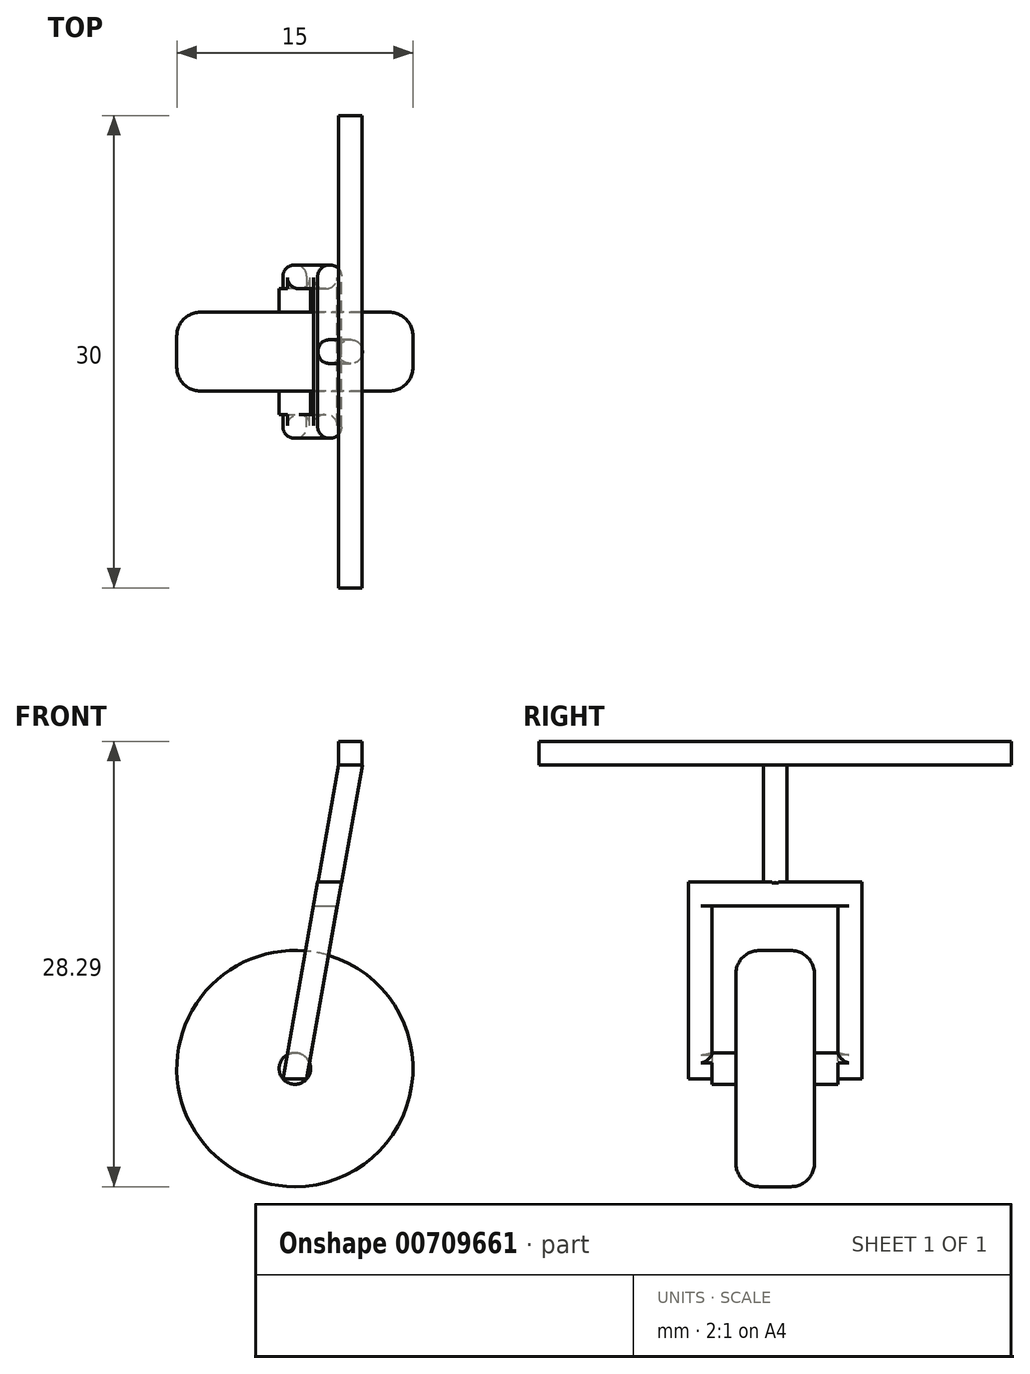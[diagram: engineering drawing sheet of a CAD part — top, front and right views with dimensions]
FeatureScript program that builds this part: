
annotation { "Feature Type Name" : "Feature", "Feature Type Description" : "" }
export const myFeature = defineFeature(function(context is Context, id is Id, definition is map)
    precondition{}
    {
        {
            var Q0;
            Q0=qCreatedBy(makeId("Front.planeOp"),FACE);
            var sketch = newSketch(context, id + "F0", { "sketchPlane" : qUnion([Q0])});
            skLineSegment(sketch, "E0.bottom", {"start": v(-45.66, 5.93) * mm, "end": v(-30.66, 5.93) * mm});
            skLineSegment(sketch, "E0.top", {"start": v(-45.66, -9.07) * mm, "end": v(-30.66, -9.07) * mm});
            skLineSegment(sketch, "E0.left", {"start": v(-45.66, 5.93) * mm, "end": v(-45.66, -9.07) * mm});
            skLineSegment(sketch, "E0.right", {"start": v(-30.66, 5.93) * mm, "end": v(-30.66, -9.07) * mm});
            skSolve(sketch);
        }
        {
            var Q0;
            Q0=makeQuery(id+"F0.imprint","IMPRINT",FACE,{"disambiguationData":[TD([[makeQuery(id+"F0.imprint","IMPRINT",EDGE,{"derivedFrom":sQuery(id+"F0.wireOp",EDGE,"E0.bottom")}),-1.0]])]});
            extrude(context, id + "F1", {"entities" : qUnion([Q0]), "endBound" : BoundingType.SYMMETRIC, "depth" : 5 * mm, "offsetDistance" : 25 * mm});
        }
        {
            var Q0;
            Q0=makeQuery(id+"F1.opExtrude","SWEPT_EDGE",EDGE,{"disambiguationData":[OSD([sQuery(id+"F0.wireOp",EDGE,"E0.bottom"),sQuery(id+"F0.wireOp",EDGE,"E0.right")])]});
            var Q1;
            Q1=makeQuery(id+"F1.opExtrude","SWEPT_EDGE",EDGE,{"disambiguationData":[OSD([sQuery(id+"F0.wireOp",EDGE,"E0.bottom"),sQuery(id+"F0.wireOp",EDGE,"E0.left")])]});
            var Q2;
            Q2=makeQuery(id+"F1.opExtrude","SWEPT_EDGE",EDGE,{"disambiguationData":[OSD([sQuery(id+"F0.wireOp",EDGE,"E0.top"),sQuery(id+"F0.wireOp",EDGE,"E0.right")])]});
            var Q3;
            Q3=makeQuery(id+"F1.opExtrude","SWEPT_EDGE",EDGE,{"disambiguationData":[OSD([sQuery(id+"F0.wireOp",EDGE,"E0.top"),sQuery(id+"F0.wireOp",EDGE,"E0.left")])]});
            fillet(context, id + "F2", {"entities" : qUnion([Q0, Q1, Q2, Q3]), "radius" : 7.5 * mm, "tangentPropagation" : true, "allowEdgeOverflow" : false});
        }
        {
            var Q0;
            {var subQ0=sQuery(id+"F0.wireOp",EDGE,"E0.left");var subQ1=sQuery(id+"F0.wireOp",EDGE,"E0.bottom");Q0=makeQuery(id+"F2.opFillet","BLEND_EDGE",EDGE,{"blendedFrom":[makeQuery(id+"F1.opExtrude","SWEPT_EDGE",EDGE,{"disambiguationData":[OSD([subQ1,subQ0])]}),makeQuery(id+"F1.opExtrude","CAP_FACE",FACE,{"disambiguationData":[OSD([subQ1,sQuery(id+"F0.wireOp",EDGE,"E0.top"),subQ0,sQuery(id+"F0.wireOp",EDGE,"E0.right")])],"isStart":false})],"blendedInto":[makeQuery(id+"F1.opExtrude","CAP_FACE",FACE,{"disambiguationData":[OSD([subQ1,sQuery(id+"F0.wireOp",EDGE,"E0.top"),subQ0,sQuery(id+"F0.wireOp",EDGE,"E0.right")])],"isStart":false})]});}
            var Q1;
            {var subQ0=sQuery(id+"F0.wireOp",EDGE,"E0.left");var subQ1=sQuery(id+"F0.wireOp",EDGE,"E0.bottom");Q1=makeQuery(id+"F2.opFillet","BLEND_EDGE",EDGE,{"blendedFrom":[makeQuery(id+"F1.opExtrude","SWEPT_EDGE",EDGE,{"disambiguationData":[OSD([subQ1,subQ0])]}),makeQuery(id+"F1.opExtrude","CAP_FACE",FACE,{"disambiguationData":[OSD([subQ1,sQuery(id+"F0.wireOp",EDGE,"E0.top"),subQ0,sQuery(id+"F0.wireOp",EDGE,"E0.right")])],"isStart":true})],"blendedInto":[makeQuery(id+"F1.opExtrude","CAP_FACE",FACE,{"disambiguationData":[OSD([subQ1,sQuery(id+"F0.wireOp",EDGE,"E0.top"),subQ0,sQuery(id+"F0.wireOp",EDGE,"E0.right")])],"isStart":true})]});}
            fillet(context, id + "F3", {"entities" : qUnion([Q0, Q1]), "radius" : 1.5 * mm, "tangentPropagation" : true, "allowEdgeOverflow" : false});
        }
        {
            var Q0;
            Q0=makeQuery(id+"F1.opExtrude","CAP_FACE",FACE,{"disambiguationData":[OSD([sQuery(id+"F0.wireOp",EDGE,"E0.bottom"),sQuery(id+"F0.wireOp",EDGE,"E0.top"),sQuery(id+"F0.wireOp",EDGE,"E0.left"),sQuery(id+"F0.wireOp",EDGE,"E0.right")])],"isStart":false});
            var sketch = newSketch(context, id + "F4", { "sketchPlane" : qUnion([Q0])});
            skCircle(sketch, "E1", {"center": v(-38.16, -1.57) * mm, "radius": 1 * mm});
            skSolve(sketch);
        }
        {
            var Q0;
            Q0=makeQuery(id+"F4.imprint","IMPRINT",FACE,{"disambiguationData":[TD([[makeQuery(id+"F4.imprint","IMPRINT",EDGE,{"derivedFrom":sQuery(id+"F4.wireOp",EDGE,"E1")}),1.0]])]});
            extrude(context, id + "F5", {"entities" : qUnion([Q0]), "operationType" : NewBodyOperationType.ADD, "depth" : 1.5 * mm, "offsetDistance" : 25 * mm});
        }
        {
            var Q0;
            Q0=makeQuery(id+"F5.opExtrude","CAP_FACE",FACE,{"disambiguationData":[OSD([sQuery(id+"F4.wireOp",EDGE,"E1")])],"isStart":false});
            var sketch = newSketch(context, id + "F6", { "sketchPlane" : qUnion([Q0])});
            skLineSegment(sketch, "E2", {"start": v(-35.21, 10.27) * mm, "end": v(-36.71, 10.27) * mm});
            skLineSegment(sketch, "E3", {"start": v(-38.91, -2.23) * mm, "end": v(-37.41, -2.23) * mm});
            skLineSegment(sketch, "E4", {"start": v(-37.41, -2.23) * mm, "end": v(-35.21, 10.27) * mm});
            skLineSegment(sketch, "E5", {"start": v(-38.91, -2.23) * mm, "end": v(-36.71, 10.27) * mm});
            skSolve(sketch);
        }
        {
            var Q0;
            {var subQ0=sQuery(id+"F6.wireOp",EDGE,"E2");Q0=makeQuery(id+"F6.imprint","IMPRINT",FACE,{"disambiguationData":[TD([[makeQuery(id+"F6.imprint","IMPRINT",EDGE,{"derivedFrom":subQ0}),1.0]])]});}
            var Q1;
            {var subQ0=sQuery(id+"F6.wireOp",EDGE,"E3");Q1=makeQuery(id+"F6.imprint","IMPRINT",FACE,{"disambiguationData":[TD([[makeQuery(id+"F6.imprint","IMPRINT",EDGE,{"derivedFrom":subQ0}),1.0]])]});}
            extrude(context, id + "F7", {"entities" : qUnion([Q0, Q1]), "operationType" : NewBodyOperationType.ADD, "depth" : 1.5 * mm, "offsetDistance" : 25 * mm});
        }
        {
            var Q0;
            Q0=makeQuery(id+"F1.opExtrude","CAP_FACE",FACE,{"disambiguationData":[OSD([sQuery(id+"F0.wireOp",EDGE,"E0.bottom"),sQuery(id+"F0.wireOp",EDGE,"E0.top"),sQuery(id+"F0.wireOp",EDGE,"E0.left"),sQuery(id+"F0.wireOp",EDGE,"E0.right")])],"isStart":true});
            var sketch = newSketch(context, id + "F8", { "sketchPlane" : qUnion([Q0])});
            skCircle(sketch, "E6", {"center": v(38.16, -1.57) * mm, "radius": 1 * mm});
            skSolve(sketch);
        }
        {
            var Q0;
            Q0=makeQuery(id+"F8.imprint","IMPRINT",FACE,{"disambiguationData":[TD([[makeQuery(id+"F8.imprint","IMPRINT",EDGE,{"derivedFrom":sQuery(id+"F8.wireOp",EDGE,"E6")}),1.0]])]});
            extrude(context, id + "F9", {"entities" : qUnion([Q0]), "operationType" : NewBodyOperationType.ADD, "depth" : 1.5 * mm, "offsetDistance" : 25 * mm});
        }
        {
            var Q0;
            Q0=makeQuery(id+"F9.opExtrude","CAP_FACE",FACE,{"disambiguationData":[OSD([sQuery(id+"F8.wireOp",EDGE,"E6")])],"isStart":false});
            var sketch = newSketch(context, id + "F10", { "sketchPlane" : qUnion([Q0])});
            skLineSegment(sketch, "E7", {"start": v(37.41, -2.23) * mm, "end": v(38.91, -2.23) * mm});
            skLineSegment(sketch, "E8", {"start": v(38.91, -2.23) * mm, "end": v(36.71, 10.27) * mm});
            skLineSegment(sketch, "E9", {"start": v(36.71, 10.27) * mm, "end": v(35.21, 10.27) * mm});
            skLineSegment(sketch, "E10", {"start": v(35.21, 10.27) * mm, "end": v(37.41, -2.23) * mm});
            skSolve(sketch);
        }
        {
            var Q0;
            {var subQ0=sQuery(id+"F10.wireOp",EDGE,"E9");Q0=makeQuery(id+"F10.imprint","IMPRINT",FACE,{"disambiguationData":[TD([[makeQuery(id+"F10.imprint","IMPRINT",EDGE,{"derivedFrom":subQ0}),1.0]])]});}
            var Q1;
            {var subQ0=sQuery(id+"F10.wireOp",EDGE,"E7");Q1=makeQuery(id+"F10.imprint","IMPRINT",FACE,{"disambiguationData":[TD([[makeQuery(id+"F10.imprint","IMPRINT",EDGE,{"derivedFrom":subQ0}),1.0]])]});}
            extrude(context, id + "F11", {"entities" : qUnion([Q0, Q1]), "operationType" : NewBodyOperationType.ADD, "depth" : 1.5 * mm, "offsetDistance" : 25 * mm});
        }
        {
            var Q0;
            Q0=makeQuery(id+"F11.opExtrude","CAP_FACE",FACE,{"disambiguationData":[OSD([sQuery(id+"F10.wireOp",EDGE,"E7"),sQuery(id+"F10.wireOp",EDGE,"E8"),sQuery(id+"F10.wireOp",EDGE,"E9"),sQuery(id+"F10.wireOp",EDGE,"E10")])],"isStart":true});
            var sketch = newSketch(context, id + "F12", { "sketchPlane" : qUnion([Q0])});
            skLineSegment(sketch, "E11.bottom", {"start": v(-36.71, 10.27) * mm, "end": v(-35.21, 10.27) * mm});
            skLineSegment(sketch, "E11.top", {"start": v(-36.97, 8.77) * mm, "end": v(-35.47, 8.77) * mm});
            skLineSegment(sketch, "E11.left", {"start": v(-36.71, 10.27) * mm, "end": v(-36.97, 8.77) * mm});
            skLineSegment(sketch, "E11.right", {"start": v(-35.21, 10.27) * mm, "end": v(-35.47, 8.77) * mm});
            skSolve(sketch);
        }
        {
            var Q0;
            Q0=makeQuery(id+"F12.imprint","IMPRINT",FACE,{"disambiguationData":[TD([[makeQuery(id+"F12.imprint","IMPRINT",EDGE,{"derivedFrom":sQuery(id+"F12.wireOp",EDGE,"E11.bottom")}),-1.0]])]});
            extrude(context, id + "F13", {"entities" : qUnion([Q0]), "operationType" : NewBodyOperationType.ADD, "depth" : 8 * mm, "offsetDistance" : 25 * mm});
        }
        {
            var Q0;
            Q0=qCreatedBy(makeId("Front.planeOp"),FACE);
            var sketch = newSketch(context, id + "F14", { "sketchPlane" : qUnion([Q0])});
            skLineSegment(sketch, "E12", {"start": v(-36.7, 10.2) * mm, "end": v(-35.2, 10.2) * mm});
            skLineSegment(sketch, "E13", {"start": v(-35.2, 10.2) * mm, "end": v(-33.88, 17.7) * mm});
            skLineSegment(sketch, "E14", {"start": v(-33.88, 17.7) * mm, "end": v(-35.38, 17.7) * mm});
            skLineSegment(sketch, "E15", {"start": v(-35.38, 17.7) * mm, "end": v(-36.7, 10.2) * mm});
            skSolve(sketch);
        }
        {
            var Q0;
            Q0=makeQuery(id+"F14.imprint","IMPRINT",FACE,{"disambiguationData":[TD([[makeQuery(id+"F14.imprint","IMPRINT",EDGE,{"derivedFrom":sQuery(id+"F14.wireOp",EDGE,"E12")}),1.0]])]});
            extrude(context, id + "F15", {"entities" : qUnion([Q0]), "operationType" : NewBodyOperationType.ADD, "endBound" : BoundingType.SYMMETRIC, "depth" : 1.5 * mm, "offsetDistance" : 25 * mm});
        }
        {
            var Q0;
            Q0=qCreatedBy(makeId("Front.planeOp"),FACE);
            var sketch = newSketch(context, id + "F16", { "sketchPlane" : qUnion([Q0])});
            skLineSegment(sketch, "E16", {"start": v(-35.4, 17.72) * mm, "end": v(-33.9, 17.72) * mm});
            skLineSegment(sketch, "E17", {"start": v(-33.9, 17.72) * mm, "end": v(-33.9, 19.22) * mm});
            skLineSegment(sketch, "E18", {"start": v(-33.9, 19.22) * mm, "end": v(-35.4, 19.22) * mm});
            skLineSegment(sketch, "E19", {"start": v(-35.4, 19.22) * mm, "end": v(-35.4, 17.72) * mm});
            skSolve(sketch);
        }
        {
            var Q0;
            Q0=makeQuery(id+"F16.imprint","IMPRINT",FACE,{"disambiguationData":[TD([[makeQuery(id+"F16.imprint","IMPRINT",EDGE,{"derivedFrom":sQuery(id+"F16.wireOp",EDGE,"E16")}),1.0]])]});
            extrude(context, id + "F17", {"entities" : qUnion([Q0]), "operationType" : NewBodyOperationType.ADD, "endBound" : BoundingType.SYMMETRIC, "depth" : 30 * mm, "offsetDistance" : 25 * mm});
        }
        {
            var Q0;
            Q0=makeQuery(id+"F7.opExtrude","CAP_EDGE",EDGE,{"disambiguationData":[OSD([sQuery(id+"F6.wireOp",EDGE,"E4")])],"isStart":false});
            var Q1;
            Q1=makeQuery(id+"F7.opExtrude","CAP_EDGE",EDGE,{"disambiguationData":[OSD([sQuery(id+"F6.wireOp",EDGE,"E5")])],"isStart":false});
            var Q2;
            {var subQ0=sQuery(id+"F6.wireOp",EDGE,"E4");Q2=makeQuery(id+"F7.boolean.opBoolean","SPLIT",EDGE,{"disambiguationData":[topologyDisambiguationEdgeConnected([makeQuery(id+"F7.opExtrude","CAP_FACE",FACE,{"disambiguationData":[OSD([sQuery(id+"F6.wireOp",EDGE,"E2"),sQuery(id+"F6.wireOp",EDGE,"E3"),subQ0,sQuery(id+"F6.wireOp",EDGE,"E5")])],"isStart":true})])],"derivedFrom":makeQuery(id+"F7.opExtrude","CAP_EDGE",EDGE,{"disambiguationData":[OSD([subQ0])],"isStart":true})});}
            var Q3;
            {var subQ0=sQuery(id+"F10.wireOp",EDGE,"E10");Q3=makeQuery(id+"F11.boolean.opBoolean","SPLIT",EDGE,{"disambiguationData":[topologyDisambiguationEdgeConnected([makeQuery(id+"F11.opExtrude","CAP_FACE",FACE,{"disambiguationData":[OSD([sQuery(id+"F10.wireOp",EDGE,"E7"),sQuery(id+"F10.wireOp",EDGE,"E8"),sQuery(id+"F10.wireOp",EDGE,"E9"),subQ0])],"isStart":true})])],"derivedFrom":makeQuery(id+"F11.opExtrude","CAP_EDGE",EDGE,{"disambiguationData":[OSD([subQ0])],"isStart":true})});}
            var Q4;
            {var subQ0=sQuery(id+"F10.wireOp",EDGE,"E8");Q4=makeQuery(id+"F11.boolean.opBoolean","SPLIT",EDGE,{"disambiguationData":[topologyDisambiguationEdgeConnected([makeQuery(id+"F11.opExtrude","CAP_FACE",FACE,{"disambiguationData":[OSD([sQuery(id+"F10.wireOp",EDGE,"E7"),subQ0,sQuery(id+"F10.wireOp",EDGE,"E9"),sQuery(id+"F10.wireOp",EDGE,"E10")])],"isStart":true})])],"derivedFrom":makeQuery(id+"F11.opExtrude","CAP_EDGE",EDGE,{"disambiguationData":[OSD([subQ0])],"isStart":true})});}
            var Q5;
            Q5=makeQuery(id+"F11.opExtrude","CAP_EDGE",EDGE,{"disambiguationData":[OSD([sQuery(id+"F10.wireOp",EDGE,"E10")])],"isStart":false});
            var Q6;
            Q6=makeQuery(id+"F11.opExtrude","CAP_EDGE",EDGE,{"disambiguationData":[OSD([sQuery(id+"F10.wireOp",EDGE,"E8")])],"isStart":false});
            var Q7;
            {var subQ0=sQuery(id+"F6.wireOp",EDGE,"E5");Q7=makeQuery(id+"F7.boolean.opBoolean","SPLIT",EDGE,{"disambiguationData":[topologyDisambiguationEdgeConnected([makeQuery(id+"F7.opExtrude","CAP_FACE",FACE,{"disambiguationData":[OSD([sQuery(id+"F6.wireOp",EDGE,"E2"),sQuery(id+"F6.wireOp",EDGE,"E3"),sQuery(id+"F6.wireOp",EDGE,"E4"),subQ0])],"isStart":true})])],"derivedFrom":makeQuery(id+"F7.opExtrude","CAP_EDGE",EDGE,{"disambiguationData":[OSD([subQ0])],"isStart":true})});}
            fillet(context, id + "F18", {"entities" : qUnion([Q0, Q1, Q2, Q3, Q4, Q5, Q6, Q7]), "radius" : 0.7 * mm, "tangentPropagation" : true, "allowEdgeOverflow" : false});
        }
        {
            var Q0;
            Q0=makeQuery(id+"F15.opExtrude","CAP_EDGE",EDGE,{"disambiguationData":[OSD([sQuery(id+"F14.wireOp",EDGE,"E13")])],"isStart":false});
            var Q1;
            Q1=makeQuery(id+"F15.opExtrude","CAP_EDGE",EDGE,{"disambiguationData":[OSD([sQuery(id+"F14.wireOp",EDGE,"E15")])],"isStart":false});
            var Q2;
            Q2=makeQuery(id+"F15.opExtrude","CAP_EDGE",EDGE,{"disambiguationData":[OSD([sQuery(id+"F14.wireOp",EDGE,"E13")])],"isStart":true});
            var Q3;
            Q3=makeQuery(id+"F15.opExtrude","CAP_EDGE",EDGE,{"disambiguationData":[OSD([sQuery(id+"F14.wireOp",EDGE,"E15")])],"isStart":true});
            fillet(context, id + "F19", {"entities" : qUnion([Q0, Q1, Q2, Q3]), "radius" : 0.7 * mm, "tangentPropagation" : true, "allowEdgeOverflow" : false});
        }
    });
